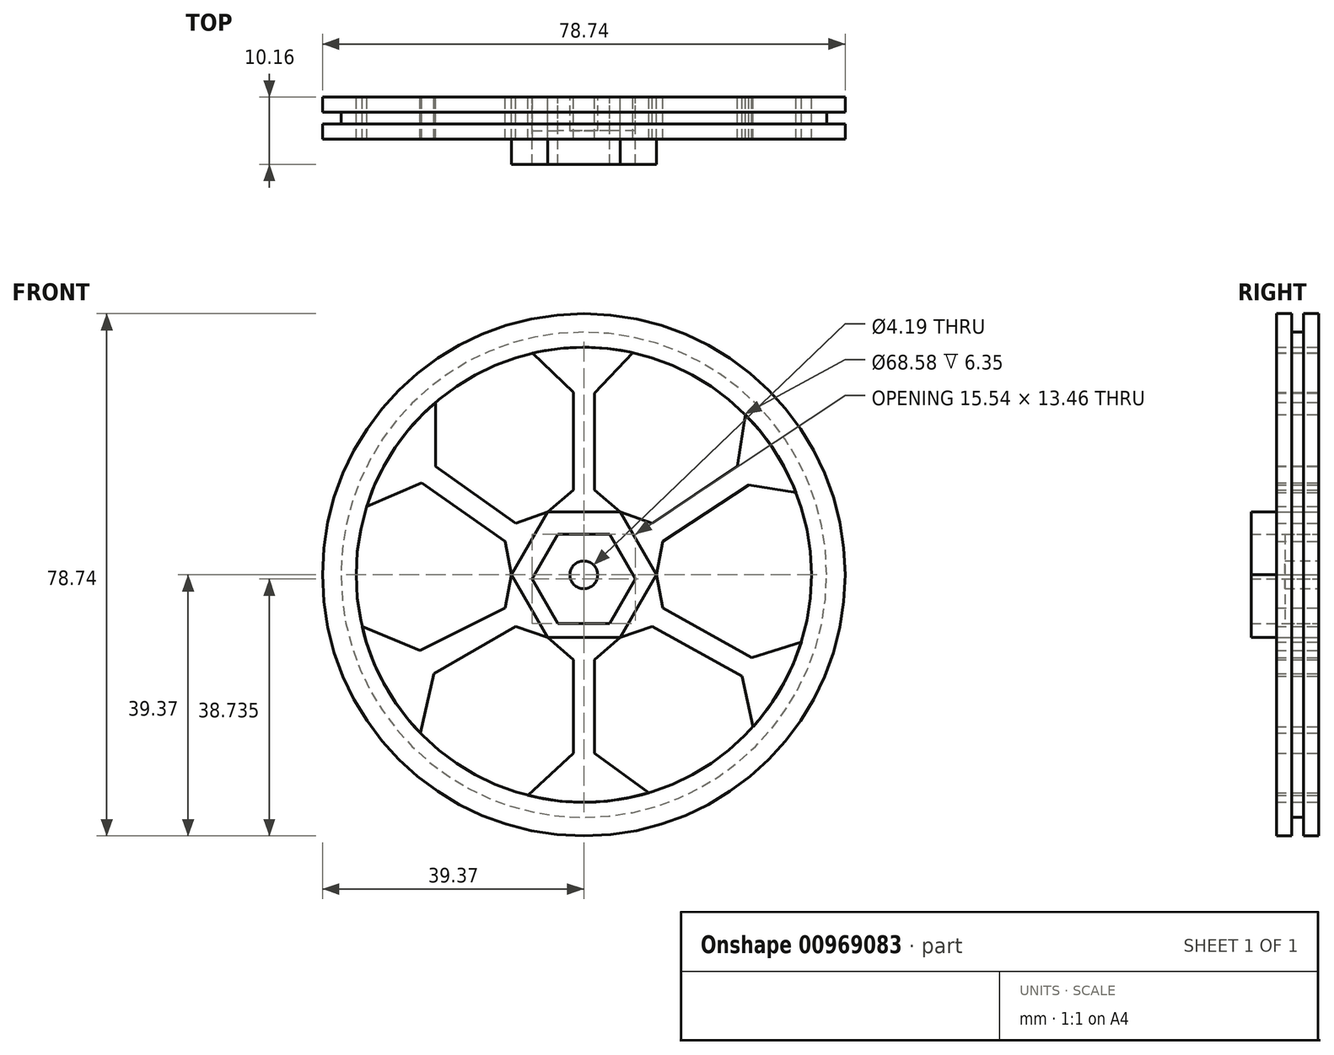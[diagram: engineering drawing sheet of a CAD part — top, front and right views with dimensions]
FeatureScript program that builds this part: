
annotation { "Feature Type Name" : "Feature", "Feature Type Description" : "" }
export const myFeature = defineFeature(function(context is Context, id is Id, definition is map)
    precondition{}
    {
        {
            var Q0;
            Q0=qCreatedBy(makeId("Front.planeOp"),FACE);
            var sketch = newSketch(context, id + "F0", { "sketchPlane" : qUnion([Q0])});
            skCircle(sketch, "E0", {"center": v(0, 0) * mm, "radius": 39.37 * mm});
            skCircle(sketch, "E1", {"center": v(0, 0) * mm, "radius": 34.3 * mm});
            skCircle(sketch, "E2", {"center": v(0, 0) * mm, "radius": 2.1 * mm});
            skLineSegment(sketch, "E3.0", {"start": v(3.89, -7.37) * mm, "end": v(-3.89, -7.37) * mm});
            skLineSegment(sketch, "E3.1", {"start": v(-3.89, -7.37) * mm, "end": v(-7.77, -0.64) * mm});
            skLineSegment(sketch, "E3.2", {"start": v(-7.77, -0.64) * mm, "end": v(-3.89, 6.1) * mm});
            skLineSegment(sketch, "E3.3", {"start": v(-3.89, 6.1) * mm, "end": v(3.89, 6.1) * mm});
            skLineSegment(sketch, "E3.4", {"start": v(3.89, 6.1) * mm, "end": v(7.77, -0.63) * mm});
            skLineSegment(sketch, "E3.5", {"start": v(7.77, -0.63) * mm, "end": v(3.89, -7.37) * mm});
            skPoint(sketch, "E3.0.midPoint", {"position": v(0, -7.37) * mm});
            skLineSegment(sketch, "E4.0", {"start": v(5.46, -9.45) * mm, "end": v(-5.46, -9.45) * mm});
            skLineSegment(sketch, "E4.1", {"start": v(-5.46, -9.45) * mm, "end": v(-10.92, 0) * mm});
            skLineSegment(sketch, "E4.2", {"start": v(-10.92, 0) * mm, "end": v(-5.46, 9.45) * mm});
            skLineSegment(sketch, "E4.3", {"start": v(-5.46, 9.45) * mm, "end": v(5.46, 9.45) * mm});
            skLineSegment(sketch, "E4.4", {"start": v(5.46, 9.45) * mm, "end": v(10.92, 0) * mm});
            skLineSegment(sketch, "E4.5", {"start": v(10.92, 0) * mm, "end": v(5.46, -9.45) * mm});
            skPoint(sketch, "E4.0.midPoint", {"position": v(0, -9.45) * mm});
            skLineSegment(sketch, "E5", {"start": v(-5.46, 9.45) * mm, "end": v(-3.89, 6.1) * mm});
            skLineSegment(sketch, "E6", {"start": v(5.46, 9.45) * mm, "end": v(3.89, 6.1) * mm});
            skLineSegment(sketch, "E7", {"start": v(10.92, 0) * mm, "end": v(7.77, -0.63) * mm});
            skLineSegment(sketch, "E8", {"start": v(5.46, -9.45) * mm, "end": v(3.89, -7.37) * mm});
            skLineSegment(sketch, "E9", {"start": v(-5.46, -9.45) * mm, "end": v(-3.89, -7.37) * mm});
            skLineSegment(sketch, "E10", {"start": v(-10.92, 0) * mm, "end": v(-7.77, -0.64) * mm});
            skLineSegment(sketch, "E11", {"start": v(-5.46, 9.45) * mm, "end": v(-1.59, 12.79) * mm});
            skLineSegment(sketch, "E12.MirrorCS", {"start": v(5.46, 9.45) * mm, "end": v(1.59, 12.79) * mm});
            skLineSegment(sketch, "E13.MirrorCS", {"start": v(5.46, -9.45) * mm, "end": v(1.59, -12.79) * mm});
            skLineSegment(sketch, "E14.MirrorCS", {"start": v(-5.46, -9.45) * mm, "end": v(-1.59, -12.79) * mm});
            skLineSegment(sketch, "E15.MirrorCS", {"start": v(-5.46, 9.45) * mm, "end": v(-10.28, 7.77) * mm});
            skLineSegment(sketch, "E16.MirrorCS", {"start": v(-10.92, 0) * mm, "end": v(-11.87, 5.02) * mm});
            skLineSegment(sketch, "E17.MirrorCS", {"start": v(-5.46, -9.45) * mm, "end": v(5.46, -9.45) * mm});
            skLineSegment(sketch, "E18.MirrorCS", {"start": v(5.46, 9.45) * mm, "end": v(10.28, 7.77) * mm});
            skLineSegment(sketch, "E19.MirrorCS", {"start": v(10.92, 0) * mm, "end": v(11.87, 5.02) * mm});
            skLineSegment(sketch, "E20.MirrorCS", {"start": v(10.92, 0) * mm, "end": v(11.87, -5.02) * mm});
            skLineSegment(sketch, "E21.MirrorCS", {"start": v(5.46, -9.45) * mm, "end": v(10.28, -7.77) * mm});
            skLineSegment(sketch, "E22.MirrorCS", {"start": v(-5.46, -9.45) * mm, "end": v(-10.28, -7.77) * mm});
            skLineSegment(sketch, "E23.MirrorCS", {"start": v(-10.92, 0) * mm, "end": v(-11.87, -5.02) * mm});
            skLineSegment(sketch, "E24", {"start": v(10.28, 7.77) * mm, "end": v(23.14, 16.39) * mm});
            skLineSegment(sketch, "E25", {"start": v(23.14, 16.39) * mm, "end": v(24.32, 24.17) * mm});
            skLineSegment(sketch, "E26", {"start": v(11.87, 5.02) * mm, "end": v(24.83, 13.52) * mm});
            skLineSegment(sketch, "E27", {"start": v(24.83, 13.52) * mm, "end": v(31.97, 12.4) * mm});
            skLineSegment(sketch, "E28", {"start": v(11.87, -5.02) * mm, "end": v(25.31, -12.48) * mm});
            skLineSegment(sketch, "E29", {"start": v(25.31, -12.48) * mm, "end": v(32.76, -10.13) * mm});
            skLineSegment(sketch, "E30", {"start": v(10.28, -7.77) * mm, "end": v(23.84, -15.28) * mm});
            skLineSegment(sketch, "E31", {"start": v(23.84, -15.28) * mm, "end": v(25.52, -22.9) * mm});
            skLineSegment(sketch, "E32", {"start": v(1.59, 12.79) * mm, "end": v(1.59, 27.37) * mm});
            skLineSegment(sketch, "E33", {"start": v(1.59, 27.37) * mm, "end": v(7.41, 33.48) * mm});
            skLineSegment(sketch, "E34", {"start": v(-1.59, 12.79) * mm, "end": v(-1.59, 27.53) * mm});
            skLineSegment(sketch, "E35", {"start": v(-1.59, 27.53) * mm, "end": v(-7.74, 33.4) * mm});
            skLineSegment(sketch, "E36", {"start": v(1.59, -12.79) * mm, "end": v(1.59, -26.88) * mm});
            skLineSegment(sketch, "E37", {"start": v(-1.59, -12.79) * mm, "end": v(-1.59, -26.89) * mm});
            skLineSegment(sketch, "E38", {"start": v(1.59, -26.88) * mm, "end": v(9.83, -32.85) * mm});
            skLineSegment(sketch, "E39", {"start": v(-1.59, -26.89) * mm, "end": v(-8.4, -33.24) * mm});
            skLineSegment(sketch, "E40", {"start": v(-11.87, -5.02) * mm, "end": v(-24.68, -11.4) * mm});
            skLineSegment(sketch, "E41", {"start": v(-24.68, -11.4) * mm, "end": v(-33.39, -7.82) * mm});
            skLineSegment(sketch, "E42", {"start": v(-10.28, -7.77) * mm, "end": v(-22.57, -14.93) * mm});
            skLineSegment(sketch, "E43", {"start": v(-22.57, -14.93) * mm, "end": v(-24.62, -23.86) * mm});
            skLineSegment(sketch, "E44", {"start": v(-10.28, 7.77) * mm, "end": v(-22.34, 16.34) * mm});
            skLineSegment(sketch, "E45", {"start": v(-22.34, 16.34) * mm, "end": v(-22.34, 26.01) * mm});
            skLineSegment(sketch, "E46", {"start": v(-11.87, 5.02) * mm, "end": v(-24.46, 13.87) * mm});
            skLineSegment(sketch, "E47", {"start": v(-24.46, 13.87) * mm, "end": v(-32.7, 10.33) * mm});
            skSolve(sketch);
        }
        {
            var Q0;
            Q0=makeQuery(id+"F0.imprint","IMPRINT",FACE,{"disambiguationData":[TD([[makeQuery(id+"F0.imprint","IMPRINT",EDGE,{"derivedFrom":sQuery(id+"F0.wireOp",EDGE,"E3.1")}),1.0]])]});
            var Q1;
            Q1=makeQuery(id+"F0.imprint","IMPRINT",FACE,{"disambiguationData":[TD([[makeQuery(id+"F0.imprint","IMPRINT",EDGE,{"derivedFrom":sQuery(id+"F0.wireOp",EDGE,"E3.2")}),1.0]])]});
            var Q2;
            Q2=makeQuery(id+"F0.imprint","IMPRINT",FACE,{"disambiguationData":[TD([[makeQuery(id+"F0.imprint","IMPRINT",EDGE,{"derivedFrom":sQuery(id+"F0.wireOp",EDGE,"E3.3")}),1.0]])]});
            var Q3;
            Q3=makeQuery(id+"F0.imprint","IMPRINT",FACE,{"disambiguationData":[TD([[makeQuery(id+"F0.imprint","IMPRINT",EDGE,{"derivedFrom":sQuery(id+"F0.wireOp",EDGE,"E3.4")}),1.0]])]});
            var Q4;
            Q4=makeQuery(id+"F0.imprint","IMPRINT",FACE,{"disambiguationData":[TD([[makeQuery(id+"F0.imprint","IMPRINT",EDGE,{"derivedFrom":sQuery(id+"F0.wireOp",EDGE,"E3.5")}),1.0]])]});
            var Q5;
            Q5=makeQuery(id+"F0.imprint","IMPRINT",FACE,{"disambiguationData":[TD([[makeQuery(id+"F0.imprint","IMPRINT",EDGE,{"derivedFrom":sQuery(id+"F0.wireOp",EDGE,"E3.0")}),1.0]])]});
            extrude(context, id + "F1", {"entities" : qUnion([Q0, Q1, Q2, Q3, Q4, Q5]), "depth" : 10.16 * mm, "offsetDistance" : 25.4 * mm});
        }
        {
            var Q0;
            Q0=makeQuery(id+"F0.imprint","IMPRINT",FACE,{"disambiguationData":[TD([[makeQuery(id+"F0.imprint","IMPRINT",EDGE,{"derivedFrom":sQuery(id+"F0.wireOp",EDGE,"E4.5")}),1.0]])]});
            var Q1;
            Q1=makeQuery(id+"F0.imprint","IMPRINT",FACE,{"disambiguationData":[TD([[makeQuery(id+"F0.imprint","IMPRINT",EDGE,{"derivedFrom":sQuery(id+"F0.wireOp",EDGE,"E4.4")}),1.0]])]});
            var Q2;
            Q2=makeQuery(id+"F0.imprint","IMPRINT",FACE,{"disambiguationData":[TD([[makeQuery(id+"F0.imprint","IMPRINT",EDGE,{"derivedFrom":sQuery(id+"F0.wireOp",EDGE,"E4.3")}),1.0]])]});
            var Q3;
            Q3=makeQuery(id+"F0.imprint","IMPRINT",FACE,{"disambiguationData":[TD([[makeQuery(id+"F0.imprint","IMPRINT",EDGE,{"derivedFrom":sQuery(id+"F0.wireOp",EDGE,"E4.2")}),1.0]])]});
            var Q4;
            Q4=makeQuery(id+"F0.imprint","IMPRINT",FACE,{"disambiguationData":[TD([[makeQuery(id+"F0.imprint","IMPRINT",EDGE,{"derivedFrom":sQuery(id+"F0.wireOp",EDGE,"E4.1")}),1.0]])]});
            var Q5;
            Q5=makeQuery(id+"F0.imprint","IMPRINT",FACE,{"disambiguationData":[TD([[makeQuery(id+"F0.imprint","IMPRINT",EDGE,{"derivedFrom":sQuery(id+"F0.wireOp",EDGE,"E14.MirrorCS")}),1.0]])]});
            extrude(context, id + "F2", {"entities" : qUnion([Q0, Q1, Q2, Q3, Q4, Q5]), "depth" : 6.35 * mm, "offsetDistance" : 25.4 * mm});
        }
        {
            var Q0;
            Q0=makeQuery(id+"F0.imprint","IMPRINT",FACE,{"disambiguationData":[TD([[makeQuery(id+"F0.imprint","IMPRINT",EDGE,{"derivedFrom":sQuery(id+"F0.wireOp",EDGE,"E0")}),1.0]])]});
            extrude(context, id + "F3", {"entities" : qUnion([Q0]), "depth" : 6.35 * mm, "offsetDistance" : 25.4 * mm});
        }
        {
            var Q0;
            Q0=makeQuery(id+"F0.imprint","IMPRINT",FACE,{"disambiguationData":[TD([[makeQuery(id+"F0.imprint","IMPRINT",EDGE,{"derivedFrom":sQuery(id+"F0.wireOp",EDGE,"E2")}),-1.0]])]});
            extrude(context, id + "F4", {"entities" : qUnion([Q0]), "depth" : 5.08 * mm, "offsetDistance" : 25.4 * mm});
        }
        {
            var Q0;
            Q0=makeQuery(id+"F3.opExtrude","SWEPT_FACE",FACE,{"disambiguationData":[OSD([sQuery(id+"F0.wireOp",EDGE,"E0")])]});
            shell(context, id + "F5", {"entities" : qUnion([Q0]), "thickness" : 2.3 * mm});
        }
    });
